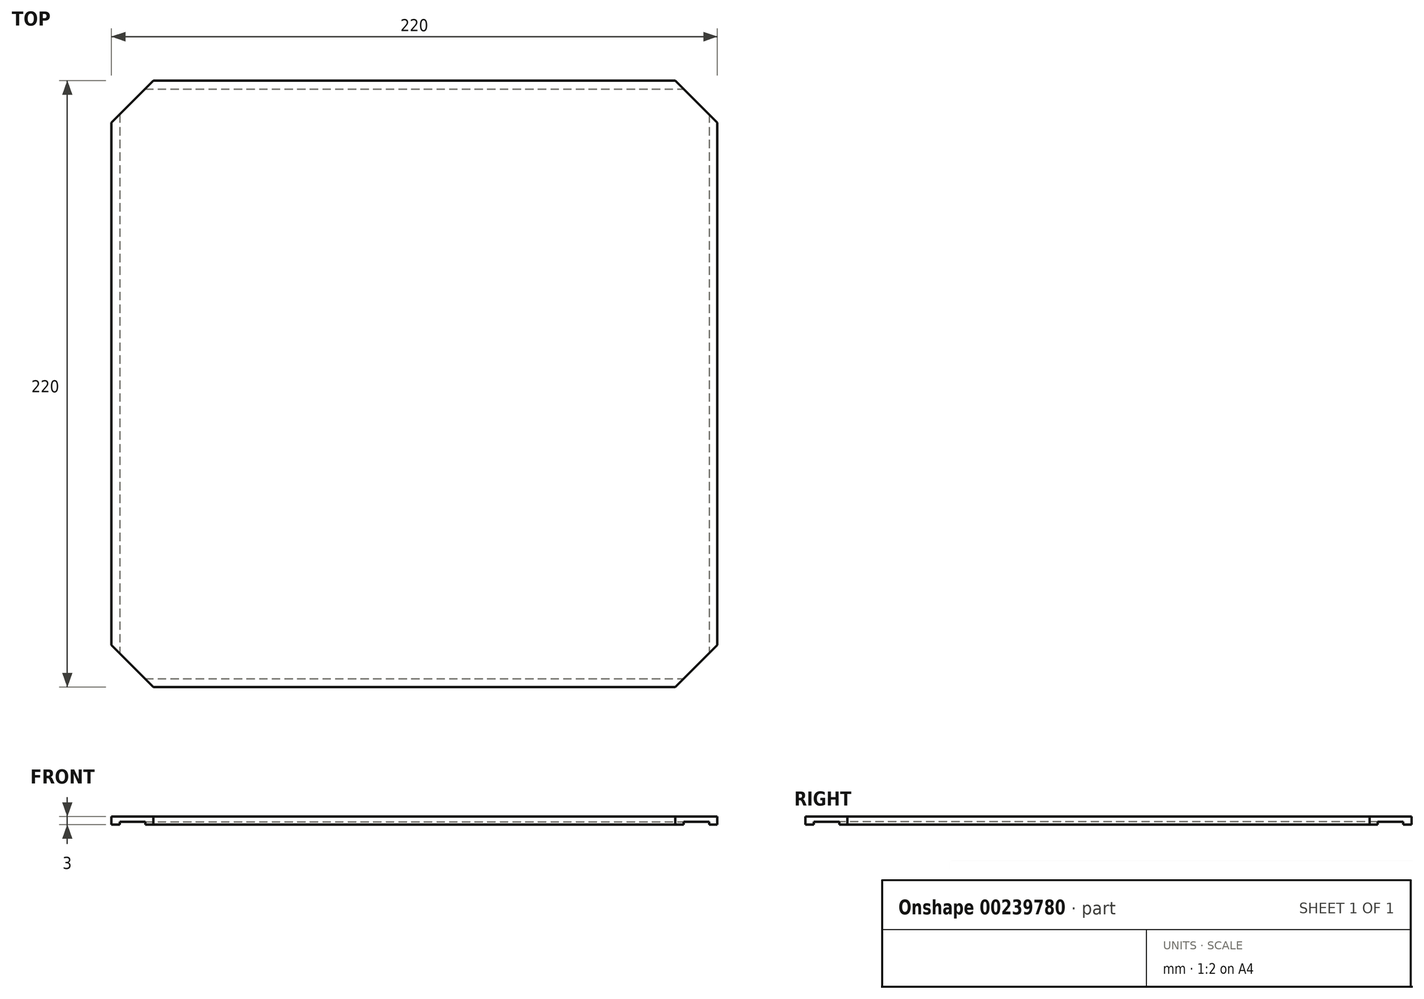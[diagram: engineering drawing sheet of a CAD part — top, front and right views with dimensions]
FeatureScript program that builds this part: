
annotation { "Feature Type Name" : "Feature", "Feature Type Description" : "" }
export const myFeature = defineFeature(function(context is Context, id is Id, definition is map)
    precondition{}
    {
        {
            var Q0;
            Q0=qCreatedBy(makeId("Top.planeOp"),FACE);
            var sketch = newSketch(context, id + "F0", { "sketchPlane" : qUnion([Q0])});
            skLineSegment(sketch, "E0.bottom", {"start": v(-104.5, -104.5) * mm, "end": v(104.5, -104.5) * mm, "construction": true});
            skLineSegment(sketch, "E0.top", {"start": v(-104.5, 104.5) * mm, "end": v(104.5, 104.5) * mm, "construction": true});
            skLineSegment(sketch, "E0.left", {"start": v(-104.5, -104.5) * mm, "end": v(-104.5, 104.5) * mm, "construction": true});
            skLineSegment(sketch, "E0.right", {"start": v(104.5, -104.5) * mm, "end": v(104.5, 104.5) * mm, "construction": true});
            skPoint(sketch, "E0.middle", {"position": v(0, 0) * mm});
            skLineSegment(sketch, "E1.bottom", {"start": v(-94.76, -110) * mm, "end": v(94.76, -110) * mm});
            skLineSegment(sketch, "E1.top", {"start": v(-94.76, 110) * mm, "end": v(94.76, 110) * mm});
            skLineSegment(sketch, "E1.left", {"start": v(-110, -94.76) * mm, "end": v(-110, 94.76) * mm});
            skLineSegment(sketch, "E1.right", {"start": v(110, -94.76) * mm, "end": v(110, 94.76) * mm});
            skCircle(sketch, "E2", {"center": v(-104.5, 104.5) * mm, "radius": 3 * mm, "construction": true});
            skLineSegment(sketch, "E3", {"start": v(-94.76, 110) * mm, "end": v(-110, 94.76) * mm});
            skLineSegment(sketch, "E4.1.0", {"start": v(-110, -94.76) * mm, "end": v(-94.76, -110) * mm});
            skLineSegment(sketch, "E4.2.0", {"start": v(94.76, -110) * mm, "end": v(110, -94.76) * mm});
            skLineSegment(sketch, "E4.3.0", {"start": v(110, 94.76) * mm, "end": v(94.76, 110) * mm});
            skPoint(sketch, "E5.orphan", {"position": v(-110, 110) * mm});
            skPoint(sketch, "E6.orphan", {"position": v(110, 110) * mm});
            skPoint(sketch, "E7.orphan", {"position": v(110, -110) * mm});
            skPoint(sketch, "E8.orphan", {"position": v(-110, -110) * mm});
            skLineSegment(sketch, "E9.bottom", {"start": v(-107, 107) * mm, "end": v(107, 107) * mm, "construction": true});
            skLineSegment(sketch, "E9.top", {"start": v(-107, -107) * mm, "end": v(107, -107) * mm, "construction": true});
            skLineSegment(sketch, "E9.left", {"start": v(-107, 107) * mm, "end": v(-107, -107) * mm, "construction": true});
            skLineSegment(sketch, "E9.right", {"start": v(107, 107) * mm, "end": v(107, -107) * mm, "construction": true});
            skSolve(sketch);
        }
        {
            var Q0;
            Q0=makeQuery(id+"F0.imprint","IMPRINT",FACE,{"disambiguationData":[TD([[makeQuery(id+"F0.imprint","IMPRINT",EDGE,{"derivedFrom":sQuery(id+"F0.wireOp",EDGE,"E1.bottom")}),1.0]])]});
            extrude(context, id + "F1", {"entities" : qUnion([Q0]), "depth" : 3 * mm});
        }
        {
            var Q0;
            Q0=qCreatedBy(makeId("Top.planeOp"),FACE);
            var sketch = newSketch(context, id + "F2", { "sketchPlane" : qUnion([Q0])});
            skLineSegment(sketch, "E10.bottom", {"start": v(-107, 107) * mm, "end": v(107, 107) * mm});
            skLineSegment(sketch, "E10.top", {"start": v(-107, -107) * mm, "end": v(107, -107) * mm});
            skLineSegment(sketch, "E10.left", {"start": v(-107, 107) * mm, "end": v(-107, -107) * mm});
            skLineSegment(sketch, "E10.right", {"start": v(107, 107) * mm, "end": v(107, -107) * mm});
            skPoint(sketch, "E10.middle", {"position": v(0, 0) * mm});
            skSolve(sketch);
        }
        {
            var Q0;
            Q0 = qSketchRegion(id + "F2", true);
            extrude(context, id + "F3", {"entities" : qUnion([Q0]), "operationType" : NewBodyOperationType.REMOVE, "depth" : 1 * mm});
        }
    });
